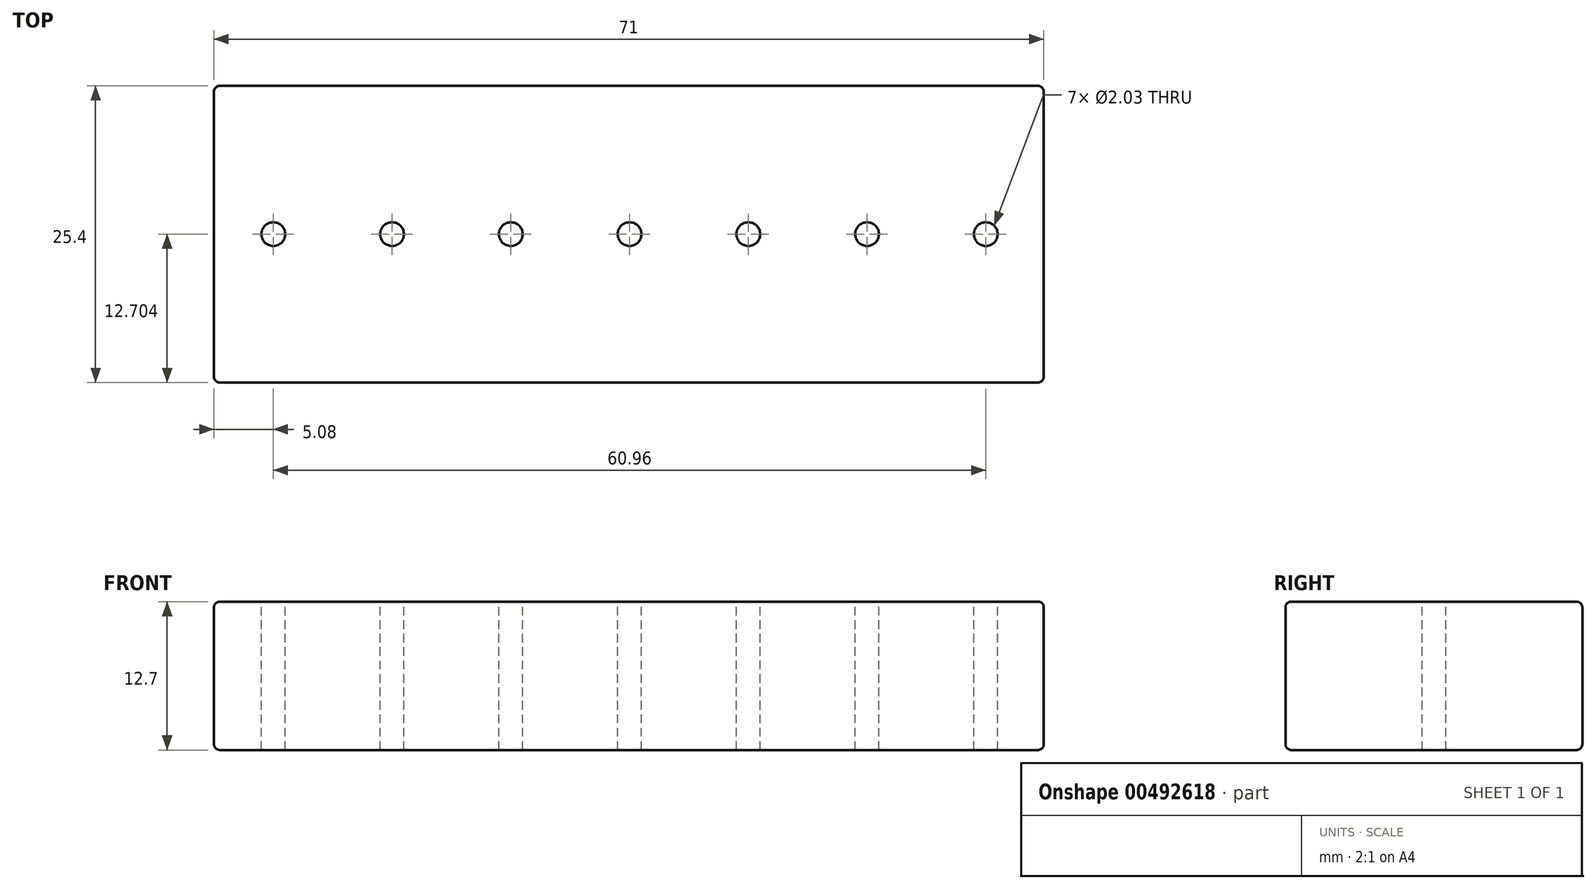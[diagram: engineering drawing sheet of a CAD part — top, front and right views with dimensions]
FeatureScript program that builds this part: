
annotation { "Feature Type Name" : "Feature", "Feature Type Description" : "" }
export const myFeature = defineFeature(function(context is Context, id is Id, definition is map)
    precondition{}
    {
        {
            var Q0;
            Q0=qCreatedBy(makeId("Top.planeOp"),FACE);
            var sketch = newSketch(context, id + "F0", { "sketchPlane" : qUnion([Q0])});
            skLineSegment(sketch, "E0", {"start": v(-61.95, 18.43) * mm, "end": v(9.05, 18.43) * mm});
            skLineSegment(sketch, "E1", {"start": v(9.05, -6.97) * mm, "end": v(-61.95, -6.97) * mm});
            skLineSegment(sketch, "E2", {"start": v(-61.95, -6.97) * mm, "end": v(-61.95, 18.43) * mm});
            skLineSegment(sketch, "E3", {"start": v(-11.15, 18.43) * mm, "end": v(-11.15, -6.97) * mm, "construction": true});
            skLineSegment(sketch, "E4", {"start": v(-11.15, 5.73) * mm, "end": v(-6.07, 5.73) * mm, "construction": true});
            skLineSegment(sketch, "E5", {"start": v(-11.15, 5.73) * mm, "end": v(-16.23, 5.73) * mm, "construction": true});
            skLineSegment(sketch, "E6", {"start": v(-6.07, 5.73) * mm, "end": v(4.09, 5.73) * mm, "construction": true});
            skLineSegment(sketch, "E7", {"start": v(3.97, 5.73) * mm, "end": v(4.09, 5.73) * mm, "construction": true});
            skLineSegment(sketch, "E8", {"start": v(3.97, 5.73) * mm, "end": v(9.05, 5.73) * mm, "construction": true});
            skLineSegment(sketch, "E9", {"start": v(-16.23, 5.73) * mm, "end": v(-26.4, 5.73) * mm, "construction": true});
            skLineSegment(sketch, "E10", {"start": v(-26.4, 5.73) * mm, "end": v(-36.55, 5.73) * mm, "construction": true});
            skLineSegment(sketch, "E11", {"start": v(-36.55, 5.73) * mm, "end": v(-46.71, 5.73) * mm, "construction": true});
            skLineSegment(sketch, "E12", {"start": v(-46.71, 5.73) * mm, "end": v(-56.87, 5.73) * mm, "construction": true});
            skCircle(sketch, "E13", {"center": v(-56.87, 5.73) * mm, "radius": 1.02 * mm});
            skCircle(sketch, "E14", {"center": v(-46.71, 5.73) * mm, "radius": 1.02 * mm});
            skCircle(sketch, "E15", {"center": v(-36.55, 5.73) * mm, "radius": 1.02 * mm});
            skCircle(sketch, "E16", {"center": v(-26.4, 5.73) * mm, "radius": 1.02 * mm});
            skCircle(sketch, "E17", {"center": v(-16.23, 5.73) * mm, "radius": 1.02 * mm});
            skCircle(sketch, "E18", {"center": v(-6.07, 5.73) * mm, "radius": 1.02 * mm});
            skCircle(sketch, "E19", {"center": v(4.09, 5.73) * mm, "radius": 1.02 * mm});
            skPoint(sketch, "E20.endSnap0", {"position": v(9.05, 5.73) * mm});
            skLineSegment(sketch, "E21", {"start": v(9.05, 18.43) * mm, "end": v(9.05, -6.97) * mm});
            skPoint(sketch, "E22.end.orphan", {"position": v(39.65, -6.97) * mm});
            skPoint(sketch, "E22.start.orphan", {"position": v(39.65, 18.43) * mm});
            skPoint(sketch, "E23.trimOffspring.end.orphan", {"position": v(14.13, 5.73) * mm});
            skSolve(sketch);
        }
        {
            var Q0;
            Q0=makeQuery(id+"F0.imprint","IMPRINT",FACE,{"disambiguationData":[TD([[makeQuery(id+"F0.imprint","IMPRINT",EDGE,{"derivedFrom":sQuery(id+"F0.wireOp",EDGE,"E0")}),-1.0]])]});
            extrude(context, id + "F1", {"entities" : qUnion([Q0]), "oppositeDirection" : true, "depth" : 12.7 * mm});
        }
        {
            var Q0;
            Q0=makeQuery(id+"F1.opExtrude","CAP_EDGE",EDGE,{"disambiguationData":[OSD([sQuery(id+"F0.wireOp",EDGE,"E0")])],"isStart":true});
            var Q1;
            Q1=makeQuery(id+"F1.opExtrude","CAP_EDGE",EDGE,{"disambiguationData":[OSD([sQuery(id+"F0.wireOp",EDGE,"E22")])],"isStart":true});
            var Q2;
            Q2=makeQuery(id+"F1.opExtrude","CAP_EDGE",EDGE,{"disambiguationData":[OSD([sQuery(id+"F0.wireOp",EDGE,"E1")])],"isStart":true});
            var Q3;
            Q3=makeQuery(id+"F1.opExtrude","CAP_EDGE",EDGE,{"disambiguationData":[OSD([sQuery(id+"F0.wireOp",EDGE,"E2")])],"isStart":true});
            var Q4;
            Q4=makeQuery(id+"F1.opExtrude","SWEPT_EDGE",EDGE,{"disambiguationData":[OSD([sQuery(id+"F0.wireOp",EDGE,"E1"),sQuery(id+"F0.wireOp",EDGE,"E2")])]});
            var Q5;
            Q5=makeQuery(id+"F1.opExtrude","SWEPT_EDGE",EDGE,{"disambiguationData":[OSD([sQuery(id+"F0.wireOp",EDGE,"E22"),sQuery(id+"F0.wireOp",EDGE,"E1")])]});
            var Q6;
            Q6=makeQuery(id+"F1.opExtrude","SWEPT_EDGE",EDGE,{"disambiguationData":[OSD([sQuery(id+"F0.wireOp",EDGE,"E0"),sQuery(id+"F0.wireOp",EDGE,"E22")])]});
            var Q7;
            Q7=makeQuery(id+"F1.opExtrude","SWEPT_EDGE",EDGE,{"disambiguationData":[OSD([sQuery(id+"F0.wireOp",EDGE,"E0"),sQuery(id+"F0.wireOp",EDGE,"E2")])]});
            var Q8;
            Q8=makeQuery(id+"F1.opExtrude","CAP_EDGE",EDGE,{"disambiguationData":[OSD([sQuery(id+"F0.wireOp",EDGE,"E22")])],"isStart":false});
            var Q9;
            Q9=makeQuery(id+"F1.opExtrude","CAP_EDGE",EDGE,{"disambiguationData":[OSD([sQuery(id+"F0.wireOp",EDGE,"E0")])],"isStart":false});
            var Q10;
            Q10=makeQuery(id+"F1.opExtrude","CAP_EDGE",EDGE,{"disambiguationData":[OSD([sQuery(id+"F0.wireOp",EDGE,"E2")])],"isStart":false});
            var Q11;
            Q11=makeQuery(id+"F1.opExtrude","CAP_EDGE",EDGE,{"disambiguationData":[OSD([sQuery(id+"F0.wireOp",EDGE,"E1")])],"isStart":false});
            var Q12;
            Q12=makeQuery(id+"F1.opExtrude","CAP_EDGE",EDGE,{"disambiguationData":[OSD([sQuery(id+"F0.wireOp",EDGE,"E21")])],"isStart":false});
            var Q13;
            Q13=makeQuery(id+"F1.opExtrude","CAP_EDGE",EDGE,{"disambiguationData":[OSD([sQuery(id+"F0.wireOp",EDGE,"E21")])],"isStart":true});
            fillet(context, id + "F2", {"entities" : qUnion([Q0, Q1, Q2, Q3, Q4, Q5, Q6, Q7, Q8, Q9, Q10, Q11, Q12, Q13]), "radius" : 0.5 * mm, "tangentPropagation" : true, "allowEdgeOverflow" : false});
        }
    });
